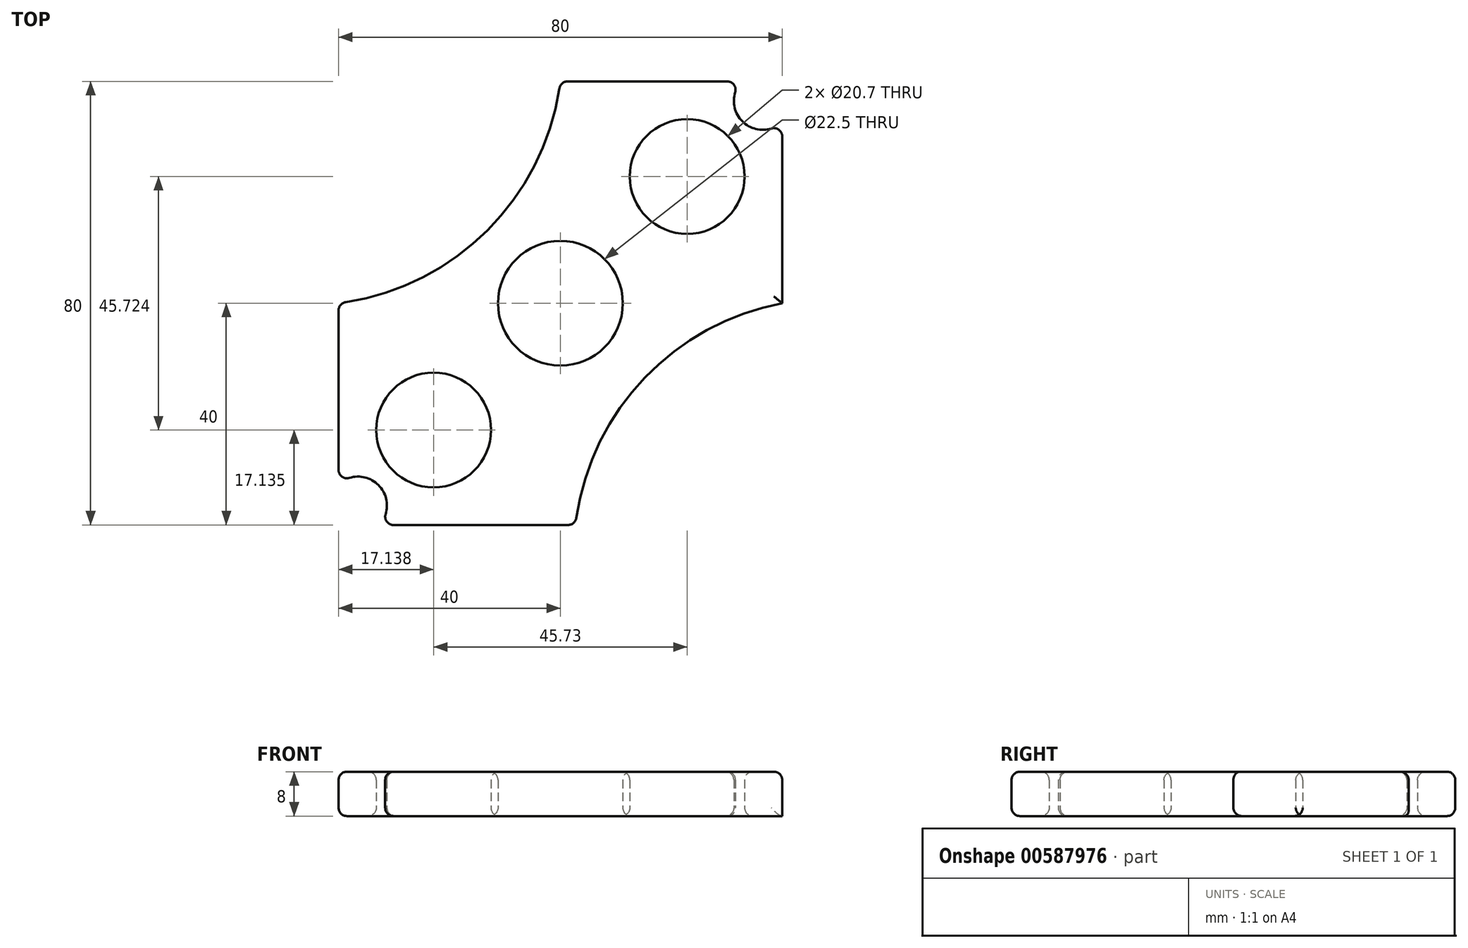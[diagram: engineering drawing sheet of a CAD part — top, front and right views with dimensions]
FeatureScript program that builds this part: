
annotation { "Feature Type Name" : "Feature", "Feature Type Description" : "" }
export const myFeature = defineFeature(function(context is Context, id is Id, definition is map)
    precondition{}
    {
        {
            var Q0;
            Q0=qCreatedBy(makeId("Top.planeOp"),FACE);
            var sketch = newSketch(context, id + "F0", { "sketchPlane" : qUnion([Q0])});
            skLineSegment(sketch, "E0.bottom", {"start": v(40, -40) * mm, "end": v(-40, -40) * mm});
            skLineSegment(sketch, "E0.top", {"start": v(40, 40) * mm, "end": v(-40, 40) * mm});
            skLineSegment(sketch, "E0.left", {"start": v(40, -40) * mm, "end": v(40, 40) * mm});
            skLineSegment(sketch, "E0.right", {"start": v(-40, -40) * mm, "end": v(-40, 40) * mm});
            skPoint(sketch, "E0.middle", {"position": v(0, 0) * mm});
            skCircle(sketch, "E1", {"center": v(-22.86, -22.86) * mm, "radius": 10.35 * mm});
            skLineSegment(sketch, "E2", {"start": v(-40, 40) * mm, "end": v(40, -40) * mm, "construction": true});
            skCircle(sketch, "E3.MirrorC", {"center": v(22.87, 22.86) * mm, "radius": 10.35 * mm});
            skLineSegment(sketch, "E4", {"start": v(40, 40) * mm, "end": v(-40, -40) * mm, "construction": true});
            skArc(sketch, "E5", {"start": v(-40, 0) * mm, "mid": v(-13.16, 13.16) * mm, "end": v(0, 40) * mm});
            skCircle(sketch, "E6", {"center": v(0, 0) * mm, "radius": 11.25 * mm});
            skArc(sketch, "E7", {"start": v(40, 0) * mm, "mid": v(14.8, -13.89) * mm, "end": v(2.7, -40) * mm});
            skArc(sketch, "E8", {"start": v(32.65, 40) * mm, "mid": v(32.8, 32.8) * mm, "end": v(40, 32.65) * mm});
            skArc(sketch, "E9.MirrorC", {"start": v(-40, -32.63) * mm, "mid": v(-32.8, -32.8) * mm, "end": v(-32.66, -40) * mm});
            skSolve(sketch);
        }
        {
            var Q0;
            Q0=makeQuery(id+"F0.imprint","IMPRINT",FACE,{"disambiguationData":[TD([[makeQuery(id+"F0.imprint","IMPRINT",EDGE,{"derivedFrom":sQuery(id+"F0.wireOp",EDGE,"E1")}),-1.0]])]});
            extrude(context, id + "F1", {"entities" : qUnion([Q0]), "depth" : 8 * mm, "offsetDistance" : 25.4 * mm});
        }
        {
            var Q0;
            Q0=makeQuery(id+"F1.opExtrude","CAP_EDGE",EDGE,{"disambiguationData":[OSD([sQuery(id+"F0.wireOp",EDGE,"E3.MirrorC")])],"isStart":false});
            var Q1;
            Q1=makeQuery(id+"F1.opExtrude","CAP_EDGE",EDGE,{"disambiguationData":[OSD([sQuery(id+"F0.wireOp",EDGE,"E6")])],"isStart":false});
            var Q2;
            Q2=makeQuery(id+"F1.opExtrude","CAP_EDGE",EDGE,{"disambiguationData":[OSD([sQuery(id+"F0.wireOp",EDGE,"E1")])],"isStart":false});
            var Q3;
            Q3=makeQuery(id+"F1.opExtrude","CAP_EDGE",EDGE,{"disambiguationData":[OSD([sQuery(id+"F0.wireOp",EDGE,"E3.MirrorC")])],"isStart":true});
            var Q4;
            Q4=makeQuery(id+"F1.opExtrude","CAP_EDGE",EDGE,{"disambiguationData":[OSD([sQuery(id+"F0.wireOp",EDGE,"E6")])],"isStart":true});
            var Q5;
            Q5=makeQuery(id+"F1.opExtrude","CAP_EDGE",EDGE,{"disambiguationData":[OSD([sQuery(id+"F0.wireOp",EDGE,"E1")])],"isStart":true});
            var Q6;
            Q6=makeQuery(id+"F1.opExtrude","CAP_EDGE",EDGE,{"disambiguationData":[OSD([sQuery(id+"F0.wireOp",EDGE,"E8")])],"isStart":false});
            var Q7;
            Q7=makeQuery(id+"F1.opExtrude","CAP_EDGE",EDGE,{"disambiguationData":[OSD([sQuery(id+"F0.wireOp",EDGE,"E0.left")])],"isStart":false});
            var Q8;
            Q8=makeQuery(id+"F1.opExtrude","CAP_EDGE",EDGE,{"disambiguationData":[OSD([sQuery(id+"F0.wireOp",EDGE,"E7")])],"isStart":false});
            var Q9;
            Q9=makeQuery(id+"F1.opExtrude","CAP_EDGE",EDGE,{"disambiguationData":[OSD([sQuery(id+"F0.wireOp",EDGE,"E0.bottom")])],"isStart":false});
            var Q10;
            Q10=makeQuery(id+"F1.opExtrude","CAP_EDGE",EDGE,{"disambiguationData":[OSD([sQuery(id+"F0.wireOp",EDGE,"E0.right")])],"isStart":false});
            var Q11;
            Q11=makeQuery(id+"F1.opExtrude","CAP_EDGE",EDGE,{"disambiguationData":[OSD([sQuery(id+"F0.wireOp",EDGE,"E9.MirrorC")])],"isStart":false});
            var Q12;
            Q12=makeQuery(id+"F1.opExtrude","CAP_EDGE",EDGE,{"disambiguationData":[OSD([sQuery(id+"F0.wireOp",EDGE,"E5")])],"isStart":false});
            var Q13;
            Q13=makeQuery(id+"F1.opExtrude","CAP_EDGE",EDGE,{"disambiguationData":[OSD([sQuery(id+"F0.wireOp",EDGE,"E0.top")])],"isStart":false});
            var Q14;
            Q14=makeQuery(id+"F1.opExtrude","SWEPT_EDGE",EDGE,{"disambiguationData":[OSD([sQuery(id+"F0.wireOp",EDGE,"E0.top"),sQuery(id+"F0.wireOp",EDGE,"E8")])]});
            var Q15;
            Q15=makeQuery(id+"F1.opExtrude","SWEPT_EDGE",EDGE,{"disambiguationData":[OSD([sQuery(id+"F0.wireOp",EDGE,"E0.left"),sQuery(id+"F0.wireOp",EDGE,"E8")])]});
            var Q16;
            Q16=makeQuery(id+"F1.opExtrude","CAP_EDGE",EDGE,{"disambiguationData":[OSD([sQuery(id+"F0.wireOp",EDGE,"E0.top")])],"isStart":true});
            var Q17;
            Q17=makeQuery(id+"F1.opExtrude","CAP_EDGE",EDGE,{"disambiguationData":[OSD([sQuery(id+"F0.wireOp",EDGE,"E5")])],"isStart":true});
            var Q18;
            Q18=makeQuery(id+"F1.opExtrude","SWEPT_EDGE",EDGE,{"disambiguationData":[OSD([sQuery(id+"F0.wireOp",EDGE,"E0.right"),sQuery(id+"F0.wireOp",EDGE,"E5")])]});
            var Q19;
            Q19=makeQuery(id+"F1.opExtrude","SWEPT_EDGE",EDGE,{"disambiguationData":[OSD([sQuery(id+"F0.wireOp",EDGE,"E0.top"),sQuery(id+"F0.wireOp",EDGE,"E5")])]});
            var Q20;
            Q20=makeQuery(id+"F1.opExtrude","CAP_EDGE",EDGE,{"disambiguationData":[OSD([sQuery(id+"F0.wireOp",EDGE,"E0.right")])],"isStart":true});
            var Q21;
            Q21=makeQuery(id+"F1.opExtrude","SWEPT_EDGE",EDGE,{"disambiguationData":[OSD([sQuery(id+"F0.wireOp",EDGE,"E0.right"),sQuery(id+"F0.wireOp",EDGE,"E9.MirrorC")])]});
            var Q22;
            Q22=makeQuery(id+"F1.opExtrude","SWEPT_EDGE",EDGE,{"disambiguationData":[OSD([sQuery(id+"F0.wireOp",EDGE,"E0.bottom"),sQuery(id+"F0.wireOp",EDGE,"E9.MirrorC")])]});
            var Q23;
            Q23=makeQuery(id+"F1.opExtrude","CAP_EDGE",EDGE,{"disambiguationData":[OSD([sQuery(id+"F0.wireOp",EDGE,"E9.MirrorC")])],"isStart":true});
            var Q24;
            Q24=makeQuery(id+"F1.opExtrude","CAP_EDGE",EDGE,{"disambiguationData":[OSD([sQuery(id+"F0.wireOp",EDGE,"E0.bottom")])],"isStart":true});
            var Q25;
            Q25=makeQuery(id+"F1.opExtrude","CAP_EDGE",EDGE,{"disambiguationData":[OSD([sQuery(id+"F0.wireOp",EDGE,"E7")])],"isStart":true});
            var Q26;
            Q26=makeQuery(id+"F1.opExtrude","SWEPT_EDGE",EDGE,{"disambiguationData":[OSD([sQuery(id+"F0.wireOp",EDGE,"E0.bottom"),sQuery(id+"F0.wireOp",EDGE,"E7")])]});
            var Q27;
            Q27=makeQuery(id+"F1.opExtrude","CAP_EDGE",EDGE,{"disambiguationData":[OSD([sQuery(id+"F0.wireOp",EDGE,"E8")])],"isStart":true});
            fillet(context, id + "F2", {"entities" : qUnion([Q0, Q1, Q2, Q3, Q4, Q5, Q6, Q7, Q8, Q9, Q10, Q11, Q12, Q13, Q14, Q15, Q16, Q17, Q18, Q19, Q20, Q21, Q22, Q23, Q24, Q25, Q26, Q27]), "radius" : 1.5 * mm, "tangentPropagation" : true, "allowEdgeOverflow" : false});
        }
    });
